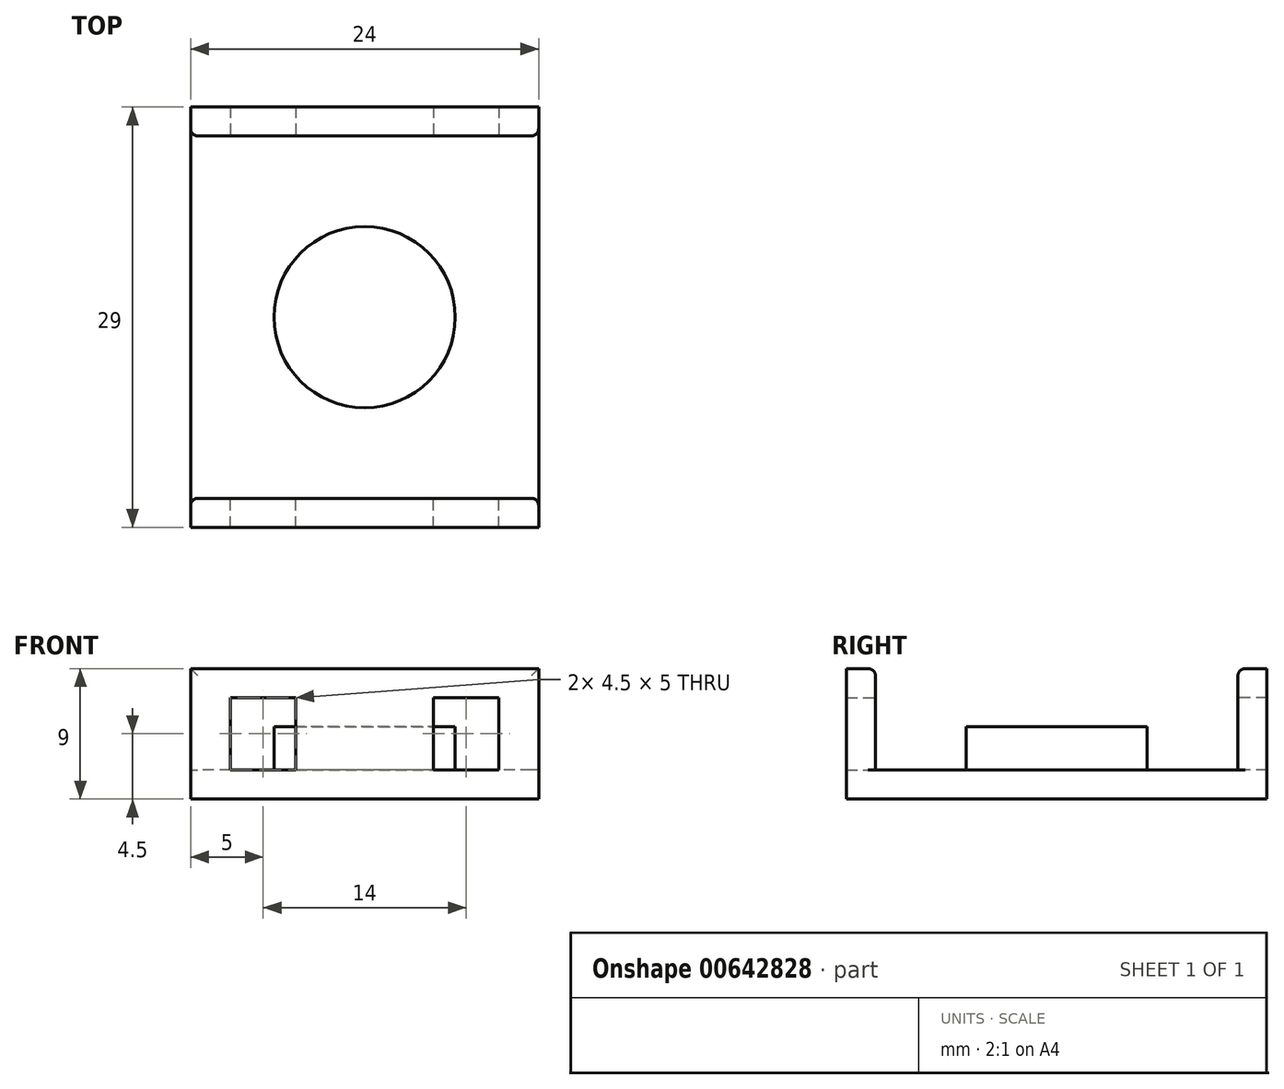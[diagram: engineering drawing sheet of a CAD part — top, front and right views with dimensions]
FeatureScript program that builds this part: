
annotation { "Feature Type Name" : "Feature", "Feature Type Description" : "" }
export const myFeature = defineFeature(function(context is Context, id is Id, definition is map)
    precondition{}
    {
        {
            var Q0;
            Q0=qCreatedBy(makeId("Top.planeOp"),FACE);
            var sketch = newSketch(context, id + "F0", { "sketchPlane" : qUnion([Q0])});
            skLineSegment(sketch, "E0.bottom", {"start": v(12, -12.5) * mm, "end": v(-12, -12.5) * mm});
            skLineSegment(sketch, "E0.top", {"start": v(12, 12.5) * mm, "end": v(-12, 12.5) * mm});
            skLineSegment(sketch, "E0.left", {"start": v(12, -12.5) * mm, "end": v(12, 12.5) * mm});
            skLineSegment(sketch, "E0.right", {"start": v(-12, -12.5) * mm, "end": v(-12, 12.5) * mm});
            skPoint(sketch, "E0.middle", {"position": v(0, 0) * mm});
            skSolve(sketch);
        }
        {
            var Q0;
            Q0=makeQuery(id+"F0.imprint","IMPRINT",FACE,{"disambiguationData":[TD([[makeQuery(id+"F0.imprint","IMPRINT",EDGE,{"derivedFrom":sQuery(id+"F0.wireOp",EDGE,"E0.bottom")}),-1.0]])]});
            extrude(context, id + "F1", {"entities" : qUnion([Q0]), "oppositeDirection" : true, "depth" : 2 * mm, "offsetDistance" : 25 * mm});
        }
        {
            var Q0;
            Q0=qCreatedBy(makeId("Top.planeOp"),FACE);
            var sketch = newSketch(context, id + "F2", { "sketchPlane" : qUnion([Q0])});
            skCircle(sketch, "E1", {"center": v(0, 0) * mm, "radius": 6.25 * mm});
            skSolve(sketch);
        }
        {
            var Q0;
            Q0 = qSketchRegion(id + "F2", true);
            extrude(context, id + "F3", {"entities" : qUnion([Q0]), "operationType" : NewBodyOperationType.ADD, "depth" : 3 * mm, "offsetDistance" : 25 * mm});
        }
        {
            var Q0;
            Q0=qCreatedBy(makeId("Top.planeOp"),FACE);
            var sketch = newSketch(context, id + "F4", { "sketchPlane" : qUnion([Q0])});
            skLineSegment(sketch, "E2.bottom", {"start": v(12, 12.5) * mm, "end": v(-12, 12.5) * mm});
            skLineSegment(sketch, "E2.top", {"start": v(12, 14.5) * mm, "end": v(-12, 14.5) * mm});
            skLineSegment(sketch, "E2.left", {"start": v(12, 12.5) * mm, "end": v(12, 14.5) * mm});
            skLineSegment(sketch, "E2.right", {"start": v(-12, 12.5) * mm, "end": v(-12, 14.5) * mm});
            skPoint(sketch, "E2.middle", {"position": v(0, 13.5) * mm});
            skLineSegment(sketch, "E3.bottom", {"start": v(12, -14.5) * mm, "end": v(-12, -14.5) * mm});
            skLineSegment(sketch, "E3.top", {"start": v(12, -12.5) * mm, "end": v(-12, -12.5) * mm});
            skLineSegment(sketch, "E3.left", {"start": v(12, -14.5) * mm, "end": v(12, -12.5) * mm});
            skLineSegment(sketch, "E3.right", {"start": v(-12, -14.5) * mm, "end": v(-12, -12.5) * mm});
            skPoint(sketch, "E3.middle", {"position": v(0, -13.5) * mm});
            skSolve(sketch);
        }
        {
            var Q0;
            Q0 = qSketchRegion(id + "F4", true);
            extrude(context, id + "F5", {"entities" : qUnion([Q0]), "operationType" : NewBodyOperationType.ADD, "depth" : 7 * mm, "offsetDistance" : 25 * mm, "hasSecondDirection" : true, "secondDirectionOppositeDirection" : true, "secondDirectionDepth" : 2 * mm});
        }
        {
            var Q0;
            Q0=qCreatedBy(makeId("Front.planeOp"),FACE);
            var sketch = newSketch(context, id + "F6", { "sketchPlane" : qUnion([Q0])});
            skLineSegment(sketch, "E4.bottom", {"start": v(-9.25, 0) * mm, "end": v(-4.75, 0) * mm});
            skLineSegment(sketch, "E4.top", {"start": v(-9.25, 5) * mm, "end": v(-4.75, 5) * mm});
            skLineSegment(sketch, "E4.left", {"start": v(-9.25, 0) * mm, "end": v(-9.25, 5) * mm});
            skLineSegment(sketch, "E4.right", {"start": v(-4.75, 0) * mm, "end": v(-4.75, 5) * mm});
            skLineSegment(sketch, "E5.bottom", {"start": v(4.75, 0) * mm, "end": v(9.25, 0) * mm});
            skLineSegment(sketch, "E5.top", {"start": v(4.75, 5) * mm, "end": v(9.25, 5) * mm});
            skLineSegment(sketch, "E5.left", {"start": v(4.75, 0) * mm, "end": v(4.75, 5) * mm});
            skLineSegment(sketch, "E5.right", {"start": v(9.25, 0) * mm, "end": v(9.25, 5) * mm});
            skSolve(sketch);
        }
        {
            var Q0;
            Q0 = qSketchRegion(id + "F6", true);
            extrude(context, id + "F7", {"entities" : qUnion([Q0]), "operationType" : NewBodyOperationType.REMOVE, "depth" : 15 * mm, "offsetDistance" : 25 * mm, "hasSecondDirection" : true, "secondDirectionOppositeDirection" : false, "secondDirectionDepth" : 12 * mm});
        }
        {
            var Q0;
            Q0 = qSketchRegion(id + "F6", true);
            extrude(context, id + "F8", {"entities" : qUnion([Q0]), "operationType" : NewBodyOperationType.REMOVE, "oppositeDirection" : true, "depth" : 15 * mm, "offsetDistance" : 25 * mm, "hasSecondDirection" : true, "secondDirectionOppositeDirection" : true, "secondDirectionDepth" : 12 * mm});
        }
        {
            var Q0;
            Q0=makeQuery(id+"F5.opExtrude","CAP_EDGE",EDGE,{"disambiguationData":[OSD([sQuery(id+"F4.wireOp",EDGE,"E3.top")])],"isStart":false});
            var Q1;
            Q1=makeQuery(id+"F5.opExtrude","CAP_EDGE",EDGE,{"disambiguationData":[OSD([sQuery(id+"F4.wireOp",EDGE,"E2.bottom")])],"isStart":false});
            var Q2;
            Q2=makeQuery(id+"F5.opExtrude","SWEPT_EDGE",EDGE,{"disambiguationData":[OSD([sQuery(id+"F4.wireOp",EDGE,"E2.bottom"),sQuery(id+"F4.wireOp",EDGE,"E2.left")])]});
            var Q3;
            Q3=makeQuery(id+"F5.opExtrude","SWEPT_EDGE",EDGE,{"disambiguationData":[OSD([sQuery(id+"F4.wireOp",EDGE,"E3.top"),sQuery(id+"F4.wireOp",EDGE,"E3.left")])]});
            var Q4;
            Q4=makeQuery(id+"F5.opExtrude","SWEPT_EDGE",EDGE,{"disambiguationData":[OSD([sQuery(id+"F4.wireOp",EDGE,"E3.top"),sQuery(id+"F4.wireOp",EDGE,"E3.right")])]});
            var Q5;
            Q5=makeQuery(id+"F5.opExtrude","SWEPT_EDGE",EDGE,{"disambiguationData":[OSD([sQuery(id+"F4.wireOp",EDGE,"E2.bottom"),sQuery(id+"F4.wireOp",EDGE,"E2.right")])]});
            fillet(context, id + "F9", {"entities" : qUnion([Q0, Q1, Q2, Q3, Q4, Q5]), "radius" : 0.5 * mm, "tangentPropagation" : true, "allowEdgeOverflow" : false});
        }
    });
